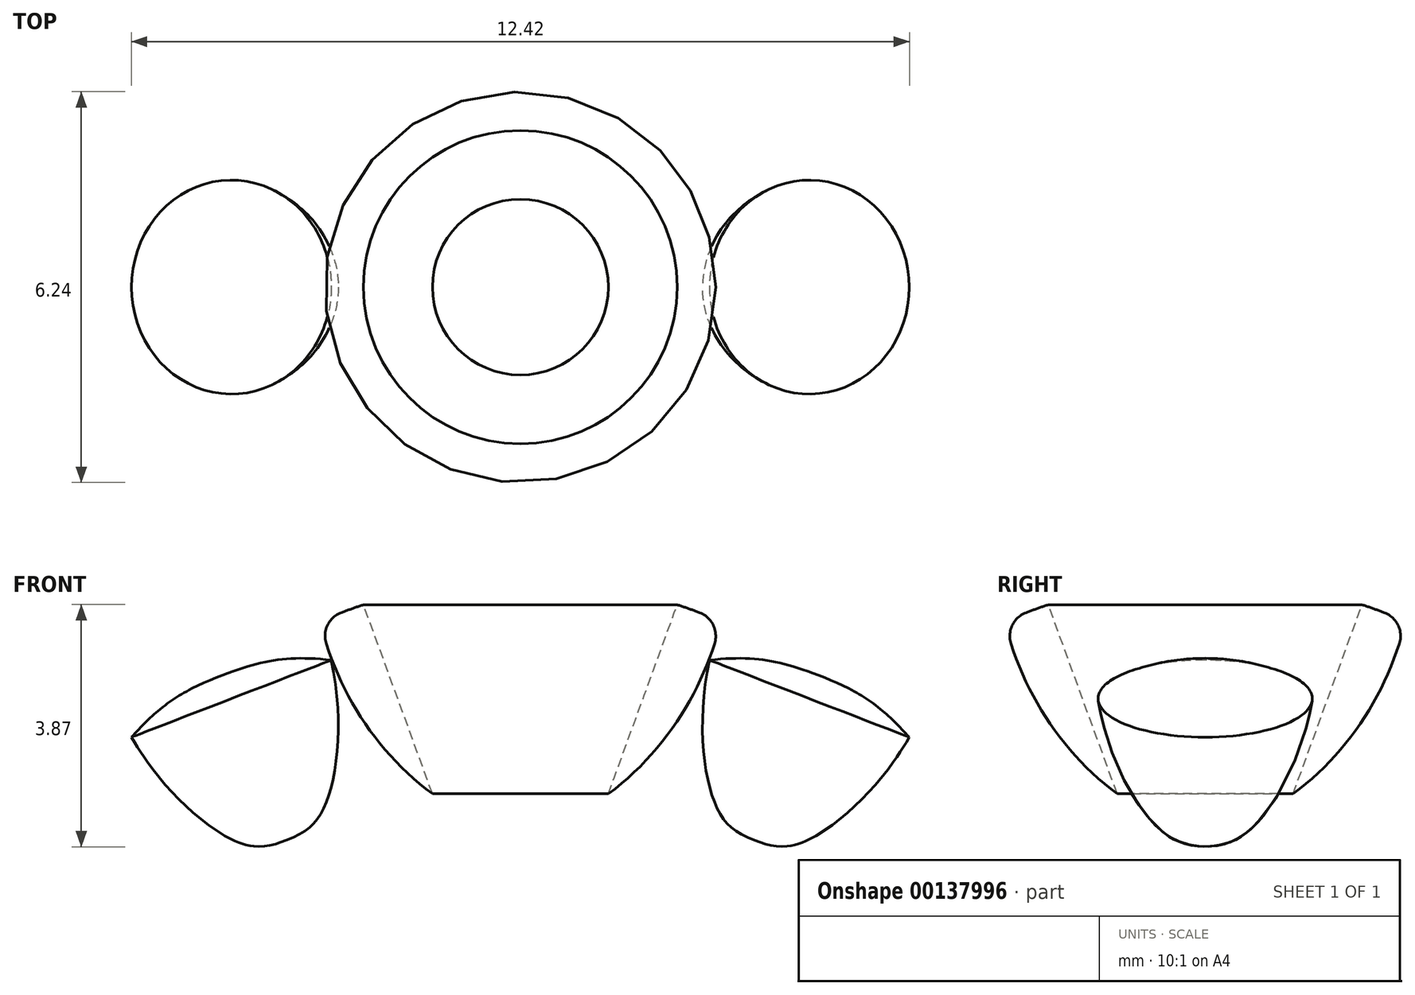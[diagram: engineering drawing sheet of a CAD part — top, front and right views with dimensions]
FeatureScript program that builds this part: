
annotation { "Feature Type Name" : "Feature", "Feature Type Description" : "" }
export const myFeature = defineFeature(function(context is Context, id is Id, definition is map)
    precondition{}
    {
        {
            var Q0;
            Q0=qCreatedBy(makeId("Front.planeOp"),FACE);
            var sketch = newSketch(context, id + "F0", { "sketchPlane" : qUnion([Q0])});
            skLineSegment(sketch, "E0", {"start": v(0, 13.82) * mm, "end": v(0, 9.82) * mm});
            skFitSpline(sketch, "E1", {"points": [v(0, 9.82) * mm, v(1.99, 10.94) * mm, v(3.23, 13.31) * mm], "startDerivative": vector(3.36, 0) * mm, "endDerivative": vector(0.97, 4.61) * mm});
            skFitSpline(sketch, "E2", {"points": [v(0, 13.82) * mm, v(1.5, 13.7) * mm, v(3.2, 13.18) * mm], "startDerivative": vector(3.1, 0) * mm, "endDerivative": vector(3.06, -1.31) * mm});
            skSolve(sketch);
        }
        {
            var Q0;
            Q0 = qSketchRegion(id + "F0", true);
            var Q1;
            Q1=sQuery(id+"F0.wireOp",EDGE,"E0");
            revolve(context, id + "F1", {"entities" : qUnion([Q0]), "axis" : qUnion([Q1]), "revolveType" : RevolveType.FULL});
        }
        {
            var Q0;
            Q0=qCreatedBy(makeId("Top.planeOp"),FACE);
            cPlane(context, id + "F2", {"entities" : qUnion([Q0]), "cplaneType" : CPlaneType.OFFSET, "offset" : 13.85 * mm, "width" : 150 * mm, "height" : 150 * mm});
        }
        {
            var Q0;
            Q0=qCreatedBy(id+"F2.planeOp",FACE);
            var sketch = newSketch(context, id + "F3", { "sketchPlane" : qUnion([Q0])});
            skCircle(sketch, "E3", {"center": v(0, 0) * mm, "radius": 2.65 * mm});
            skSolve(sketch);
        }
        {
            var Q0;
            Q0 = qSketchRegion(id + "F3", true);
            extrude(context, id + "F4", {"entities" : qUnion([Q0]), "operationType" : NewBodyOperationType.REMOVE, "oppositeDirection" : true, "depth" : 25 * mm, "hasDraft" : true, "draftAngle" : 20 * degree, "draftPullDirection" : true});
        }
        {
            var Q0;
            Q0=makeQuery(id+"F1.opRevolve","SWEPT_EDGE",EDGE,{"disambiguationData":[OSD([sQuery(id+"F0.wireOp",EDGE,"E1"),sQuery(id+"F0.wireOp",EDGE,"E2")])]});
            fillet(context, id + "F5", {"entities" : qUnion([Q0]), "radius" : .4 * mm, "tangentPropagation" : true, "allowEdgeOverflow" : false});
        }
        {
            var Q0;
            Q0=qCreatedBy(makeId("Front.planeOp"),FACE);
            var sketch = newSketch(context, id + "F6", { "sketchPlane" : qUnion([Q0])});
            skLineSegment(sketch, "E4", {"start": v(0, 0) * mm, "end": v(0, 14.33) * mm, "construction": true});
            skLineSegment(sketch, "E5", {"start": v(0, 0) * mm, "end": v(-4.76, 12.32) * mm, "construction": true});
            skLineSegment(sketch, "E6", {"start": v(-4.76, 12.32) * mm, "end": v(-3.74, 9.68) * mm});
            skFitSpline(sketch, "E7", {"points": [v(-3.74, 9.68) * mm, v(-3.11, 10.26) * mm, v(-3.02, 12.56) * mm], "startDerivative": vector(2.72, 1.05) * mm, "endDerivative": vector(-0.97, 4.47) * mm});
            skFitSpline(sketch, "E8", {"points": [v(-3.02, 12.56) * mm, v(-3.9, 12.56) * mm, v(-4.76, 12.32) * mm], "startDerivative": vector(-2.08, 0.24) * mm, "endDerivative": vector(-2.07, -0.8) * mm});
            skSolve(sketch);
        }
        {
            var Q0;
            Q0 = qSketchRegion(id + "F6", true);
            var Q1;
            Q1=sQuery(id+"F6.wireOp",EDGE,"E5");
            revolve(context, id + "F7", {"operationType" : NewBodyOperationType.ADD, "entities" : qUnion([Q0]), "axis" : qUnion([Q1]), "revolveType" : RevolveType.FULL});
        }
        {
            var Q0;
            Q0=makeQuery(id+"F7.opRevolve","SWEPT_BODY",BODY,{"disambiguationData":[OSD([sQuery(id+"F6.wireOp",EDGE,"E6"),sQuery(id+"F6.wireOp",EDGE,"E7"),sQuery(id+"F6.wireOp",EDGE,"E8")])]});
            var Q1;
            Q1=qCreatedBy(makeId("Right.planeOp"),FACE);
            mirror(context, id + "F8", {"entities" : qUnion([Q0]), "mirrorPlane" : qUnion([Q1])});
        }
    });
